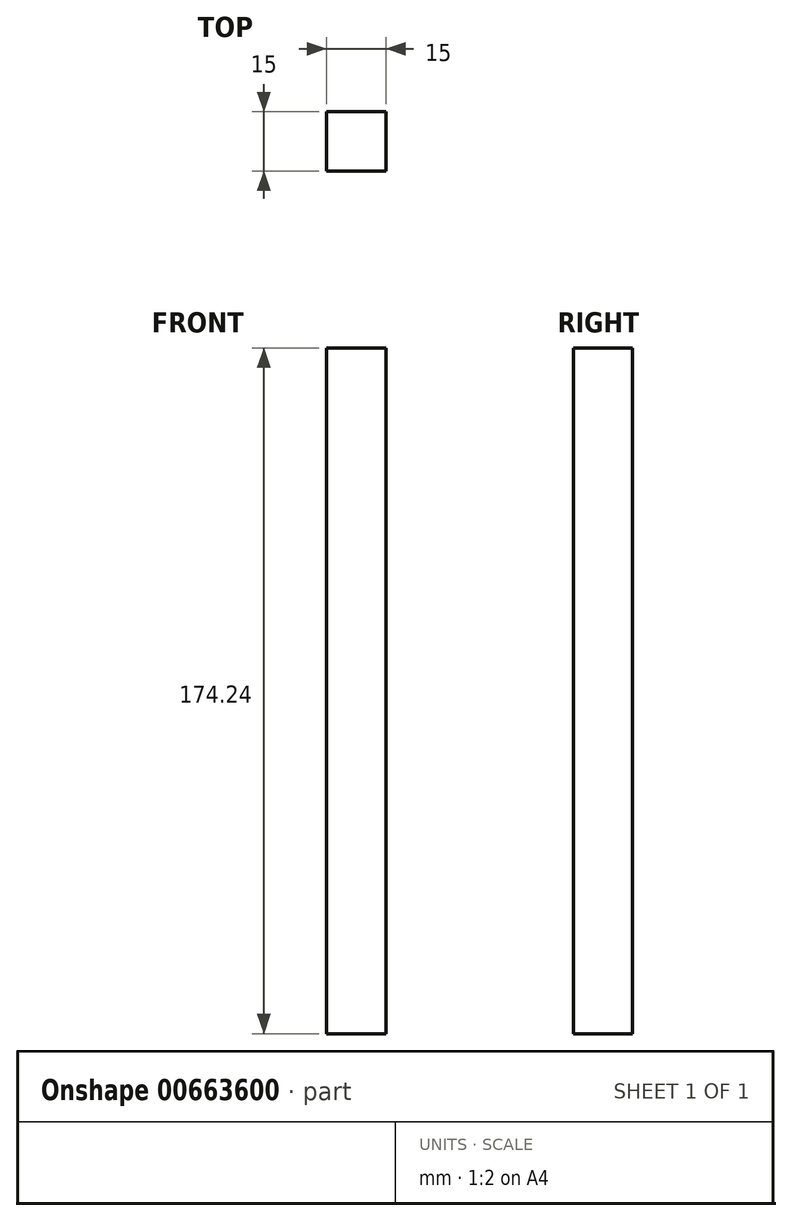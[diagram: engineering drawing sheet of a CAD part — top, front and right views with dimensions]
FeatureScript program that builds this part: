
annotation { "Feature Type Name" : "Feature", "Feature Type Description" : "" }
export const myFeature = defineFeature(function(context is Context, id is Id, definition is map)
    precondition{}
    {
        {
            var Q0;
            Q0=qCreatedBy(makeId("Top.planeOp"),FACE);
            var sketch = newSketch(context, id + "F0", { "sketchPlane" : qUnion([Q0])});
            skLineSegment(sketch, "E0.bottom", {"start": v(71.63, 7.5) * mm, "end": v(-71.63, 7.5) * mm});
            skLineSegment(sketch, "E0.top", {"start": v(71.63, -7.5) * mm, "end": v(-71.63, -7.5) * mm});
            skLineSegment(sketch, "E0.left", {"start": v(71.63, 7.5) * mm, "end": v(71.63, -7.5) * mm});
            skLineSegment(sketch, "E0.right", {"start": v(-71.63, 7.5) * mm, "end": v(-71.63, -7.5) * mm});
            skPoint(sketch, "E0.middle", {"position": v(0, 0) * mm});
            skLineSegment(sketch, "E1.bottom", {"start": v(7.5, 71.63) * mm, "end": v(-7.5, 71.63) * mm});
            skLineSegment(sketch, "E1.top", {"start": v(7.5, -71.63) * mm, "end": v(-7.5, -71.63) * mm});
            skLineSegment(sketch, "E1.left", {"start": v(7.5, 71.63) * mm, "end": v(7.5, -71.63) * mm});
            skLineSegment(sketch, "E1.right", {"start": v(-7.5, 71.63) * mm, "end": v(-7.5, -71.63) * mm});
            skSolve(sketch);
        }
        {
            var Q0;
            {var subQ0=sQuery(id+"F0.wireOp",EDGE,"E1.left");var subQ1=sQuery(id+"F0.wireOp",EDGE,"E0.bottom");var subQ2=makeQuery(id+"F0.imprint","INTERSECT",VERTEX,{"derivedFrom":[subQ1,subQ0]});Q0=makeQuery(id+"F0.imprint","IMPRINT",FACE,{"disambiguationData":[TD([[makeQuery(id+"F0.imprint","IMPRINT",EDGE,{"disambiguationData":[TD([[subQ2,-1.0]])],"derivedFrom":subQ1}),1.0]])]});}
            extrude(context, id + "F1", {"entities" : qUnion([Q0]), "endBound" : BoundingType.SYMMETRIC, "depth" : 174.25 * mm, "offsetDistance" : 25 * mm});
        }
    });
